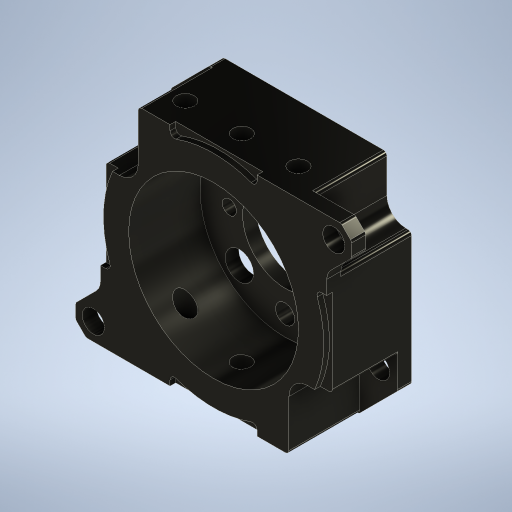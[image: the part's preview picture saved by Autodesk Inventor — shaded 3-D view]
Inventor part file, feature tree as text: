
AUTODESK INVENTOR PART (.ipt)
format: ipt  version: 2024 (Build 280153000, 153)  size: 378,368 bytes
history: native  units: in
note: dims shown in document units (in); Inventor stores cm internally (conversion verified against a paired STEP export)
features: fillet x1
ambient origin geometry x8: Origin, YZ Plane, XZ Plane, XY Plane, X Axis, Y Axis, Z Axis, Center Point
bodies: Solid1 (feature_tree)
feature tree (1):
  fillet  "Fillet5"  [1 undecoded]
note: 1 required parameter value undecoded (feature->parameter linkage not recoverable at this tier; creation-order binding heuristic only, values carry confidence <= 0.55)
